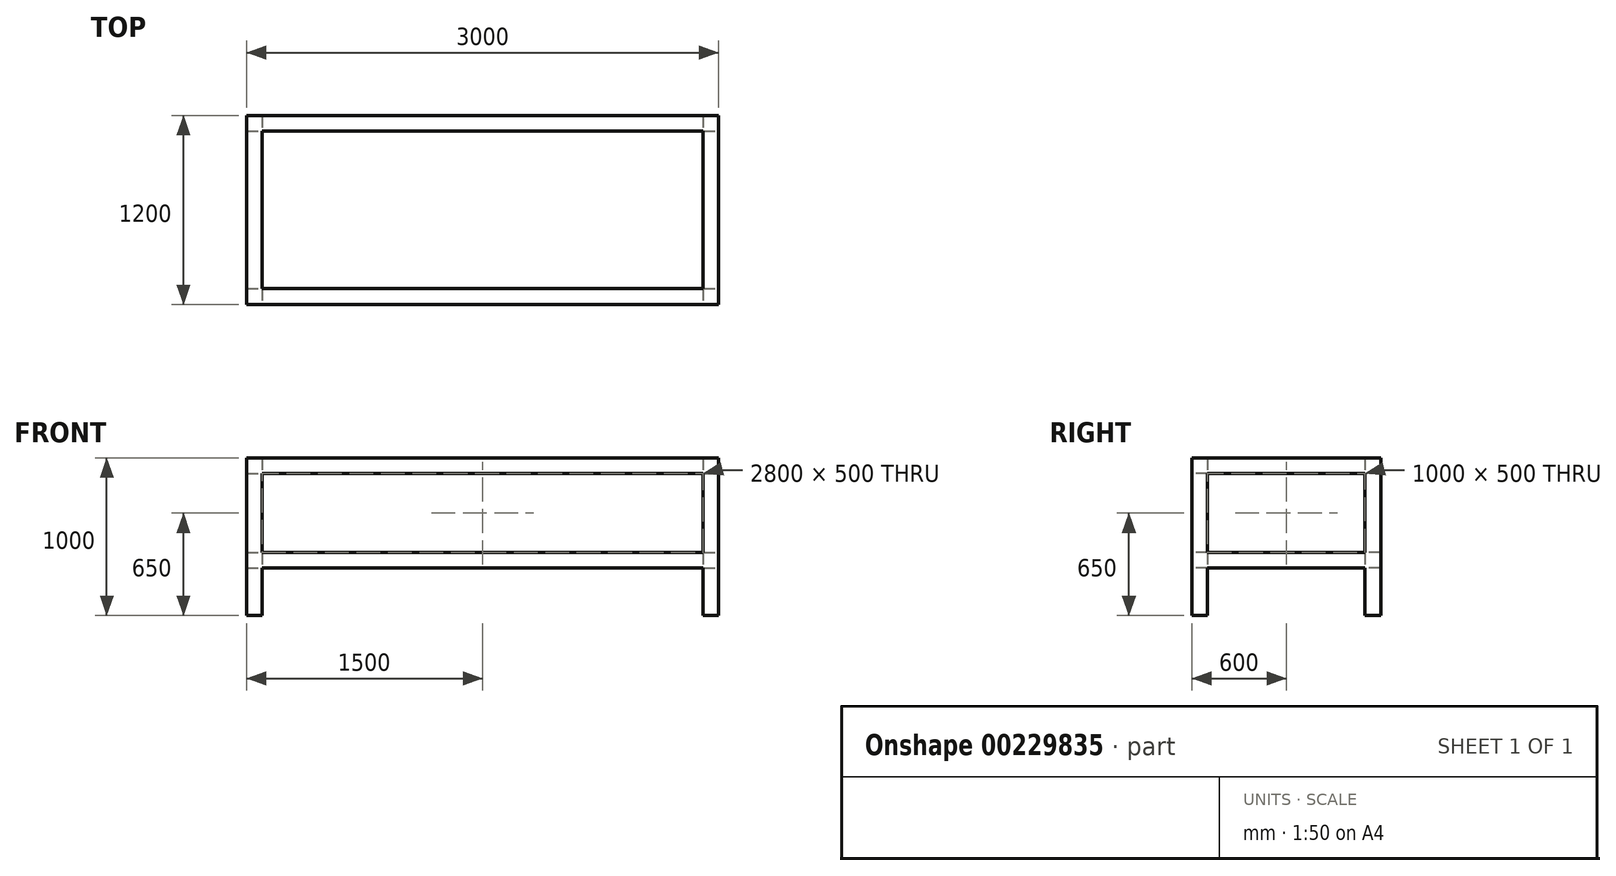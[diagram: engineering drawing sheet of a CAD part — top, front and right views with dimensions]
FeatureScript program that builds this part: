
annotation { "Feature Type Name" : "Feature", "Feature Type Description" : "" }
export const myFeature = defineFeature(function(context is Context, id is Id, definition is map)
    precondition{}
    {
        {
            var Q0;
            Q0=qCreatedBy(makeId("Top.planeOp"),FACE);
            var sketch = newSketch(context, id + "F0", { "sketchPlane" : qUnion([Q0])});
            skLineSegment(sketch, "E0.bottom", {"start": v(-1500, 600) * mm, "end": v(1500, 600) * mm});
            skLineSegment(sketch, "E0.top", {"start": v(-1500, -600) * mm, "end": v(1500, -600) * mm});
            skLineSegment(sketch, "E0.left", {"start": v(-1500, 600) * mm, "end": v(-1500, -600) * mm});
            skLineSegment(sketch, "E0.right", {"start": v(1500, 600) * mm, "end": v(1500, -600) * mm});
            skLineSegment(sketch, "E1.0", {"start": v(-1400, 500) * mm, "end": v(1400, 500) * mm});
            skLineSegment(sketch, "E1.1", {"start": v(-1400, 500) * mm, "end": v(-1400, -500) * mm});
            skLineSegment(sketch, "E1.2", {"start": v(-1400, -500) * mm, "end": v(1400, -500) * mm});
            skLineSegment(sketch, "E1.3", {"start": v(1400, 500) * mm, "end": v(1400, -500) * mm});
            skSolve(sketch);
        }
        {
            var Q0;
            Q0=makeQuery(id+"F0.imprint","IMPRINT",FACE,{"disambiguationData":[TD([[makeQuery(id+"F0.imprint","IMPRINT",EDGE,{"derivedFrom":sQuery(id+"F0.wireOp",EDGE,"E0.bottom")}),-1.0]])]});
            extrude(context, id + "F1", {"entities" : qUnion([Q0]), "depth" : 1000 * mm});
        }
        {
            var Q0;
            Q0=qCreatedBy(makeId("Front.planeOp"),FACE);
            var sketch = newSketch(context, id + "F2", { "sketchPlane" : qUnion([Q0])});
            skLineSegment(sketch, "E2.bottom", {"start": v(-1400, 900) * mm, "end": v(1400, 900) * mm});
            skLineSegment(sketch, "E2.top", {"start": v(-1400, 400) * mm, "end": v(1400, 400) * mm});
            skLineSegment(sketch, "E2.left", {"start": v(-1400, 900) * mm, "end": v(-1400, 400) * mm});
            skLineSegment(sketch, "E2.right", {"start": v(1400, 900) * mm, "end": v(1400, 400) * mm});
            skLineSegment(sketch, "E3.bottom", {"start": v(-1400, 300) * mm, "end": v(1400, 300) * mm});
            skLineSegment(sketch, "E3.top", {"start": v(-1400, 0) * mm, "end": v(1400, 0) * mm});
            skLineSegment(sketch, "E3.left", {"start": v(-1400, 300) * mm, "end": v(-1400, 0) * mm});
            skLineSegment(sketch, "E3.right", {"start": v(1400, 300) * mm, "end": v(1400, 0) * mm});
            skSolve(sketch);
        }
        {
            var Q0;
            Q0=makeQuery(id+"F2.imprint","IMPRINT",FACE,{"disambiguationData":[TD([[makeQuery(id+"F2.imprint","IMPRINT",EDGE,{"derivedFrom":sQuery(id+"F2.wireOp",EDGE,"E2.bottom")}),-1.0]])]});
            var Q1;
            Q1=makeQuery(id+"F2.imprint","IMPRINT",FACE,{"disambiguationData":[TD([[makeQuery(id+"F2.imprint","IMPRINT",EDGE,{"derivedFrom":sQuery(id+"F2.wireOp",EDGE,"E3.bottom")}),-1.0]])]});
            extrude(context, id + "F3", {"entities" : qUnion([Q0, Q1]), "operationType" : NewBodyOperationType.REMOVE, "endBound" : BoundingType.THROUGH_ALL, "oppositeDirection" : true, "depth" : 25 * mm, "hasSecondDirection" : true, "secondDirectionBound" : SecondDirectionBoundingType.THROUGH_ALL, "secondDirectionOppositeDirection" : false, "secondDirectionDepth" : 25 * mm});
        }
        {
            var Q0;
            Q0=qCreatedBy(makeId("Right.planeOp"),FACE);
            var sketch = newSketch(context, id + "F4", { "sketchPlane" : qUnion([Q0])});
            skLineSegment(sketch, "E4.bottom", {"start": v(500, 900) * mm, "end": v(-500, 900) * mm});
            skLineSegment(sketch, "E4.top", {"start": v(500, 400) * mm, "end": v(-500, 400) * mm});
            skLineSegment(sketch, "E4.left", {"start": v(500, 900) * mm, "end": v(500, 400) * mm});
            skLineSegment(sketch, "E4.right", {"start": v(-500, 900) * mm, "end": v(-500, 400) * mm});
            skLineSegment(sketch, "E5.bottom", {"start": v(500, 300) * mm, "end": v(-500, 300) * mm});
            skLineSegment(sketch, "E5.top", {"start": v(500, 0) * mm, "end": v(-500, 0) * mm});
            skLineSegment(sketch, "E5.left", {"start": v(500, 300) * mm, "end": v(500, 0) * mm});
            skLineSegment(sketch, "E5.right", {"start": v(-500, 300) * mm, "end": v(-500, 0) * mm});
            skSolve(sketch);
        }
        {
            var Q0;
            Q0=makeQuery(id+"F4.imprint","IMPRINT",FACE,{"disambiguationData":[TD([[makeQuery(id+"F4.imprint","IMPRINT",EDGE,{"derivedFrom":sQuery(id+"F4.wireOp",EDGE,"E4.bottom")}),1.0]])]});
            var Q1;
            Q1=makeQuery(id+"F4.imprint","IMPRINT",FACE,{"disambiguationData":[TD([[makeQuery(id+"F4.imprint","IMPRINT",EDGE,{"derivedFrom":sQuery(id+"F4.wireOp",EDGE,"E5.bottom")}),1.0]])]});
            extrude(context, id + "F5", {"entities" : qUnion([Q0, Q1]), "operationType" : NewBodyOperationType.REMOVE, "endBound" : BoundingType.THROUGH_ALL, "oppositeDirection" : true, "depth" : 25 * mm, "hasSecondDirection" : true, "secondDirectionBound" : SecondDirectionBoundingType.THROUGH_ALL, "secondDirectionOppositeDirection" : false, "secondDirectionDepth" : 25 * mm});
        }
    });
